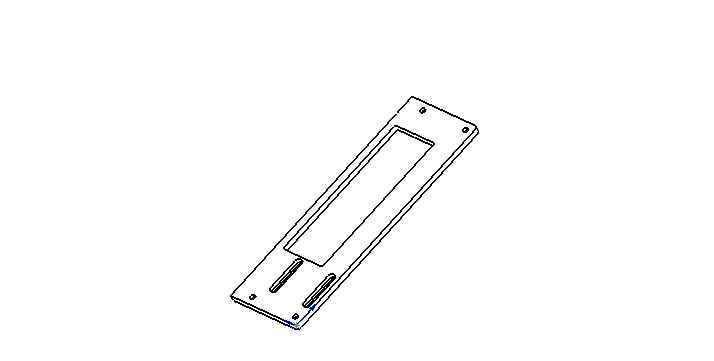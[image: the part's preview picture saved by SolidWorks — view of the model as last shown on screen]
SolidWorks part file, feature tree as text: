
SOLIDWORKS PART (.sldprt)
format: sldprt  version: not decoded by parser v0  size: 366,080 bytes
history: native  units: mm
features: sketch x4, cut_extrude x2, extrude x1 (+11 scaffold rows collapsed)
feature tree (18):
  scaffold x11  (default folders/planes/origin — collapsed)
  sketch  "Sketch1"  dims[c1.D11=4.953mm c1.D12=4.953mm c1.D13=4.9276mm c1.D14=4.9276mm c1.D15=3.175mm c1.D16=1.5875mm c1.D18=4.9276mm c1.D19=4.9276mm c1.D20=4.9276mm c1.D21=4.9276mm c2.D20=6.35mm c2.D1=~394.49375mm c2.D2=127.0mm c2.D3=76.2mm c2.D4=244.475mm c2.D5=50.8mm c2.D6=12.7mm c2.D7=12.7mm c2.D8=12.7mm c2.D9=12.7mm c2.D10=31.75mm c2.D17=76.2mm c2.D18=~51.59375mm c2.D19=38.1mm]
  extrude  "Extrude1"  Depth=9.525mm
  sketch  "Sketch2"  dims[D1=7.9502mm D2=7.9502mm D3=7.9502mm D4=7.9502mm]
  cut_extrude  "Cut-Extrude1"  Depth=4.7625mm
  sketch  "Sketch3"  dims[D1=3.8862mm D2=3.8862mm]
  cut_extrude  "Cut-Extrude2"  Depth=6.35mm
  sketch  "Sketch4"
decode coverage: 6 of 7 modeling features carry decoded parameters
note: ~ marks probable driven/reference dimensions
note: suppression state not decoded; provenance and decode notes live in map.json
